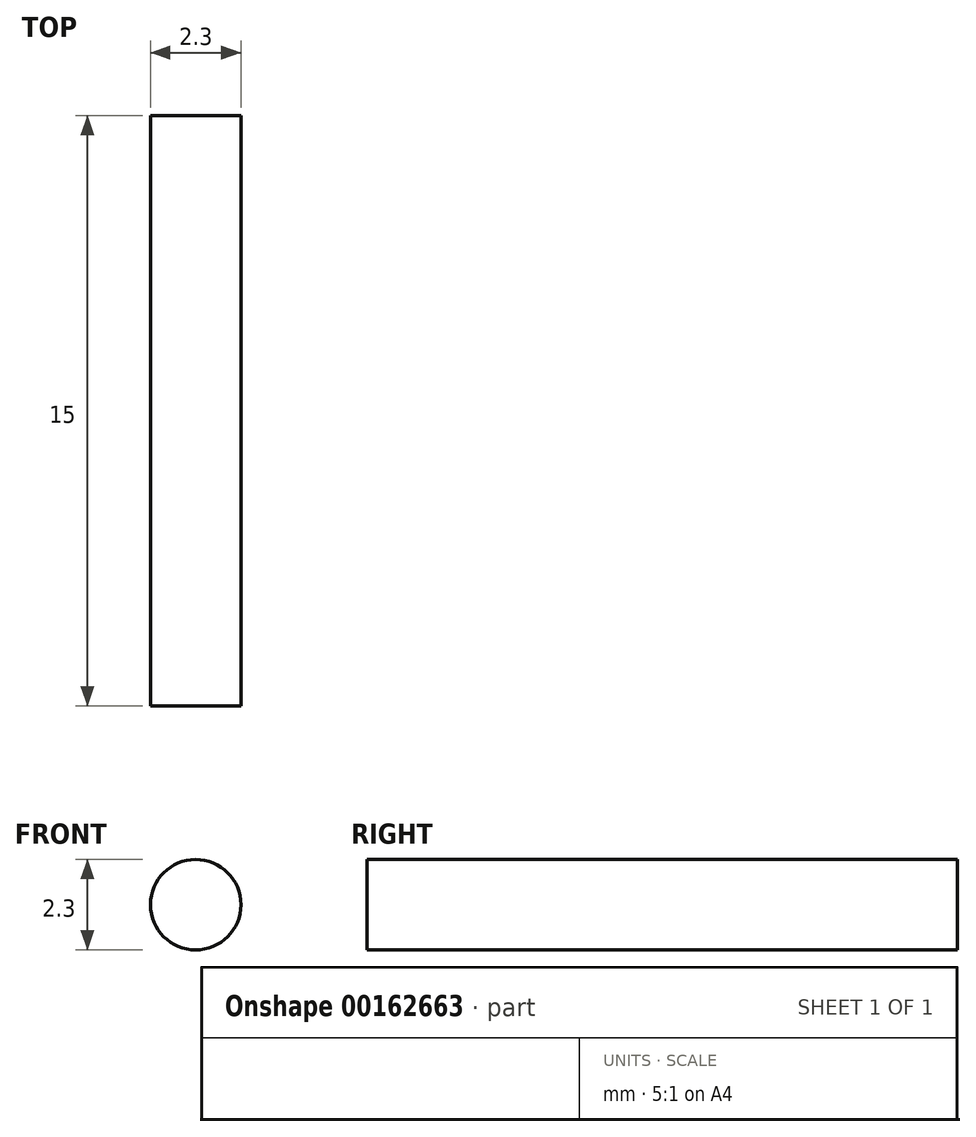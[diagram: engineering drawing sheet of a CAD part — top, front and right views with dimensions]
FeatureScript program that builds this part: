
annotation { "Feature Type Name" : "Feature", "Feature Type Description" : "" }
export const myFeature = defineFeature(function(context is Context, id is Id, definition is map)
    precondition{}
    {
        {
            var Q0;
            Q0=qCreatedBy(makeId("Front.planeOp"),FACE);
            var sketch = newSketch(context, id + "F0", { "sketchPlane" : qUnion([Q0])});
            skCircle(sketch, "E0", {"center": v(0, 0) * mm, "radius": 1.15 * mm});
            skSolve(sketch);
        }
        {
            var Q0;
            Q0 = qSketchRegion(id + "F0", true);
            extrude(context, id + "F1", {"entities" : qUnion([Q0]), "depth" : 15 * mm, "offsetDistance" : 25 * mm});
        }
    });
